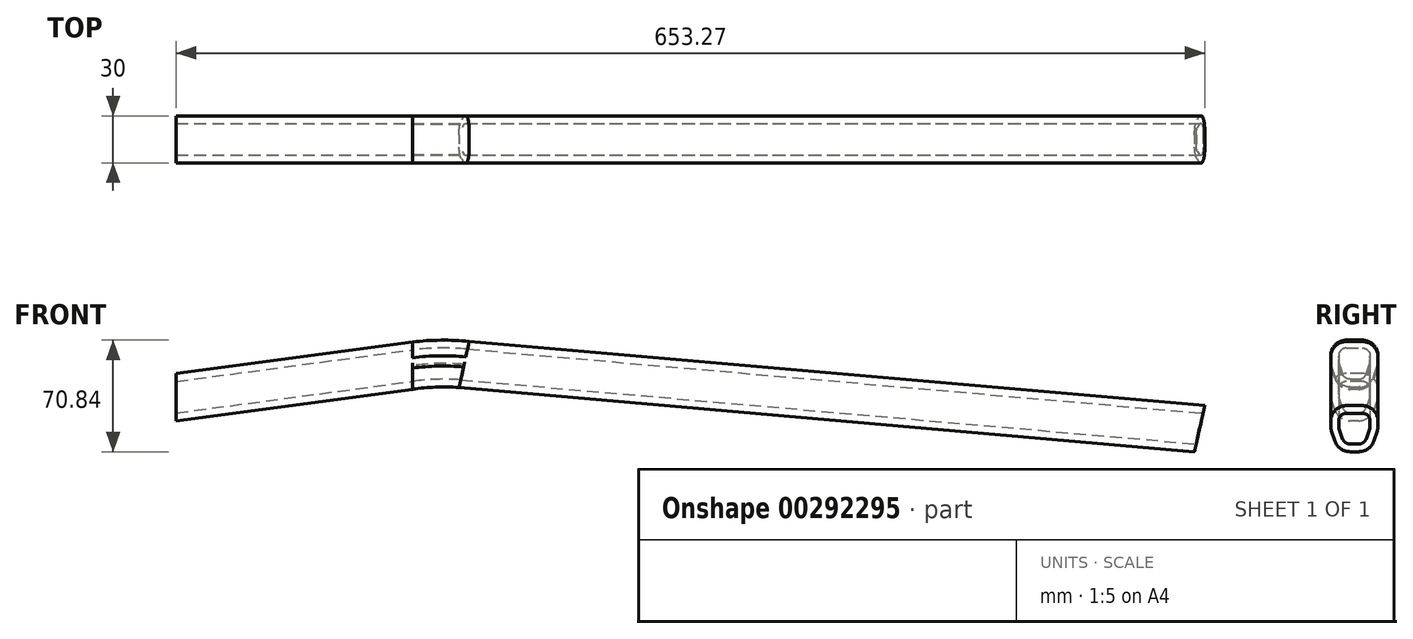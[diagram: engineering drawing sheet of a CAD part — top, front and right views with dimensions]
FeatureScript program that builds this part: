
annotation { "Feature Type Name" : "Feature", "Feature Type Description" : "" }
export const myFeature = defineFeature(function(context is Context, id is Id, definition is map)
    precondition{}
    {
        {
            var Q0;
            Q0=qCreatedBy(makeId("Front.planeOp"),FACE);
            var sketch = newSketch(context, id + "F0", { "sketchPlane" : qUnion([Q0])});
            skLineSegment(sketch, "E0", {"start": v(0, 0) * mm, "end": v(150, 20) * mm});
            skArc(sketch, "E1", {"start": v(150, 20) * mm, "mid": v(166.4, 21.28) * mm, "end": v(182.86, 20.75) * mm});
            skLineSegment(sketch, "E2", {"start": v(182.86, 20.75) * mm, "end": v(650, -20) * mm});
            skSolve(sketch);
        }
        {
            var Q0;
            Q0=qCreatedBy(makeId("Right.planeOp"),FACE);
            var sketch = newSketch(context, id + "F1", { "sketchPlane" : qUnion([Q0])});
            skLineSegment(sketch, "E3", {"start": v(5, 15) * mm, "end": v(-5, 15) * mm});
            skLineSegment(sketch, "E4", {"start": v(15, 5) * mm, "end": v(15, 1.62) * mm});
            skLineSegment(sketch, "E5", {"start": v(14.49, -1.54) * mm, "end": v(12.28, -8.16) * mm});
            skLineSegment(sketch, "E6", {"start": v(2.8, -15) * mm, "end": v(-2.8, -15) * mm});
            skLineSegment(sketch, "E7", {"start": v(-12.28, -8.16) * mm, "end": v(-14.49, -1.54) * mm});
            skLineSegment(sketch, "E8", {"start": v(-15, 1.62) * mm, "end": v(-15, 5) * mm});
            skPoint(sketch, "E9.visualSharp", {"position": v(15, 15) * mm});
            skArc(sketch, "E9.filletArc", {"start": v(15, 5) * mm, "mid": v(12.07, 12.07) * mm, "end": v(5, 15) * mm});
            skPoint(sketch, "E10.visualSharp", {"position": v(-15, 15) * mm});
            skArc(sketch, "E10.filletArc", {"start": v(-5, 15) * mm, "mid": v(-12.07, 12.07) * mm, "end": v(-15, 5) * mm});
            skPoint(sketch, "E11.visualSharp", {"position": v(-15, 0) * mm});
            skArc(sketch, "E11.filletArc", {"start": v(-15, 1.62) * mm, "mid": v(-14.87, 0.02) * mm, "end": v(-14.49, -1.54) * mm});
            skPoint(sketch, "E12.visualSharp", {"position": v(15, 0) * mm});
            skArc(sketch, "E12.filletArc", {"start": v(14.49, -1.54) * mm, "mid": v(14.87, 0.02) * mm, "end": v(15, 1.62) * mm});
            skPoint(sketch, "E13.visualSharp", {"position": v(10, -15) * mm});
            skArc(sketch, "E13.filletArc", {"start": v(2.8, -15) * mm, "mid": v(8.64, -13.11) * mm, "end": v(12.28, -8.16) * mm});
            skPoint(sketch, "E14.visualSharp", {"position": v(-10, -15) * mm});
            skArc(sketch, "E14.filletArc", {"start": v(-12.28, -8.16) * mm, "mid": v(-8.64, -13.11) * mm, "end": v(-2.8, -15) * mm});
            skArc(sketch, "E15.0", {"start": v(10, 5) * mm, "mid": v(8.54, 8.54) * mm, "end": v(5, 10) * mm});
            skLineSegment(sketch, "E15.1", {"start": v(-7.54, -6.58) * mm, "end": v(-9.74, 0.04) * mm});
            skArc(sketch, "E15.2", {"start": v(-10, 1.62) * mm, "mid": v(-9.94, 0.82) * mm, "end": v(-9.74, 0.04) * mm});
            skLineSegment(sketch, "E15.3", {"start": v(-10, 1.62) * mm, "end": v(-10, 5) * mm});
            skArc(sketch, "E15.4", {"start": v(-5, 10) * mm, "mid": v(-8.54, 8.54) * mm, "end": v(-10, 5) * mm});
            skArc(sketch, "E15.5", {"start": v(-7.54, -6.58) * mm, "mid": v(-5.72, -9.06) * mm, "end": v(-2.8, -10) * mm});
            skLineSegment(sketch, "E15.6", {"start": v(5, 10) * mm, "end": v(-5, 10) * mm});
            skLineSegment(sketch, "E15.7", {"start": v(2.8, -10) * mm, "end": v(-2.8, -10) * mm});
            skArc(sketch, "E15.8", {"start": v(2.8, -10) * mm, "mid": v(5.72, -9.06) * mm, "end": v(7.54, -6.58) * mm});
            skLineSegment(sketch, "E15.9", {"start": v(9.74, 0.04) * mm, "end": v(7.54, -6.58) * mm});
            skArc(sketch, "E15.10", {"start": v(9.74, 0.04) * mm, "mid": v(9.94, 0.82) * mm, "end": v(10, 1.62) * mm});
            skLineSegment(sketch, "E15.11", {"start": v(10, 5) * mm, "end": v(10, 1.62) * mm});
            skSolve(sketch);
        }
        {
            var Q0;
            Q0 = qSketchRegion(id + "F1", true);
            var Q1;
            Q1 = qConstructionFilter(qBodyType(qCreatedBy(id + "F0" ,EDGE), BodyType.WIRE), ConstructionObject.NO);
            sweep(context, id + "F2", {"profiles" : qUnion([Q0]), "path" : qUnion([Q1])});
        }
    });
